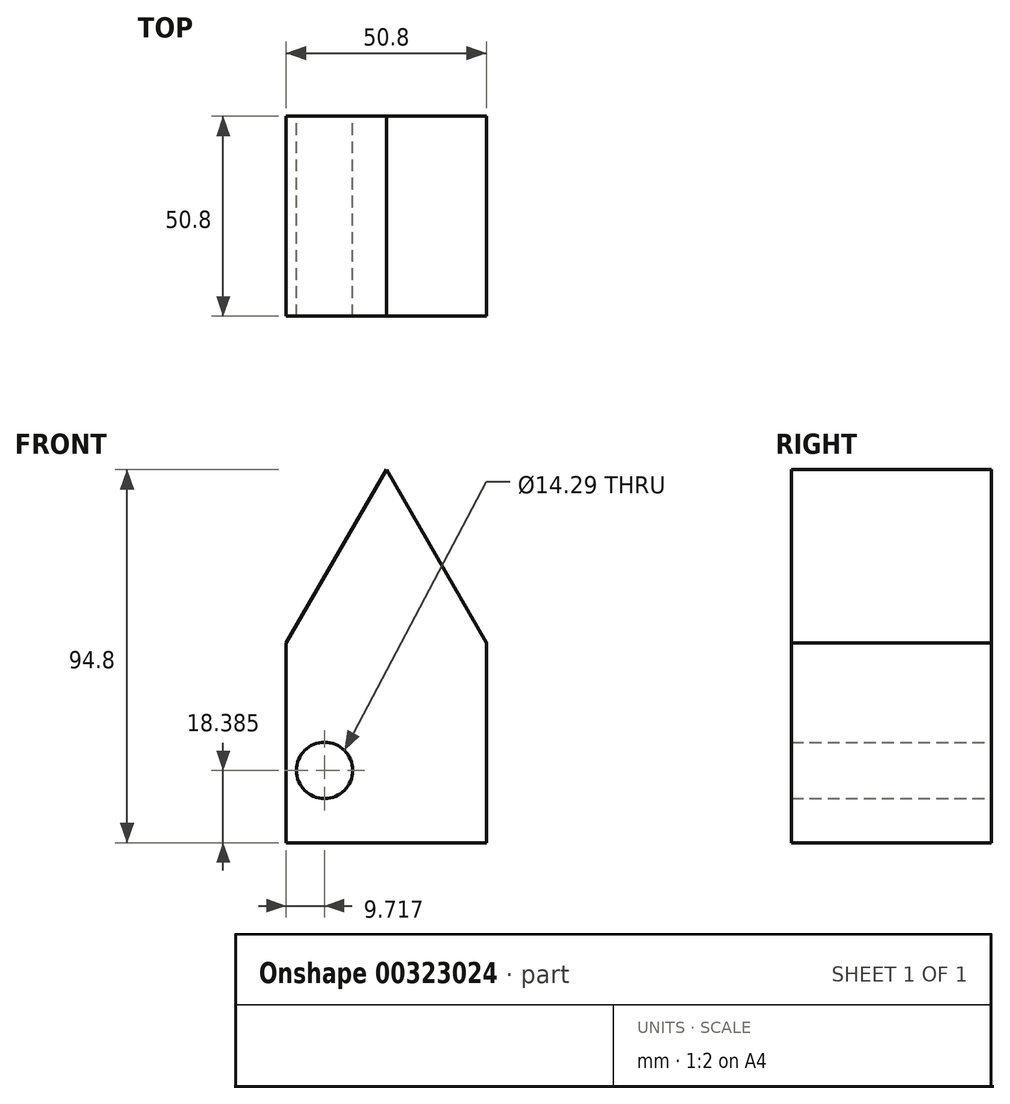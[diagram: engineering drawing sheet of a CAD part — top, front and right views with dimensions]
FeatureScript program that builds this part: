
annotation { "Feature Type Name" : "Feature", "Feature Type Description" : "" }
export const myFeature = defineFeature(function(context is Context, id is Id, definition is map)
    precondition{}
    {
        {
            var Q0;
            Q0=qCreatedBy(makeId("Front.planeOp"),FACE);
            var sketch = newSketch(context, id + "F0", { "sketchPlane" : qUnion([Q0])});
            skLineSegment(sketch, "E0.top", {"start": v(-25.4, -26.88) * mm, "end": v(25.4, -26.88) * mm});
            skLineSegment(sketch, "E0.left", {"start": v(-25.4, 23.92) * mm, "end": v(-25.4, -26.88) * mm});
            skLineSegment(sketch, "E0.right", {"start": v(25.4, 23.92) * mm, "end": v(25.4, -26.88) * mm});
            skLineSegment(sketch, "E1", {"start": v(-25.4, 23.92) * mm, "end": v(0, 67.92) * mm});
            skLineSegment(sketch, "E2", {"start": v(0, 67.92) * mm, "end": v(25.4, 23.92) * mm});
            skCircle(sketch, "E3", {"center": v(-15.68, -8.5) * mm, "radius": 7.14 * mm});
            skSolve(sketch);
        }
        {
            var Q0;
            Q0=makeQuery(id+"F0.imprint","IMPRINT",FACE,{"disambiguationData":[TD([[makeQuery(id+"F0.imprint","IMPRINT",EDGE,{"derivedFrom":sQuery(id+"F0.wireOp",EDGE,"E0.top")}),1.0]])]});
            extrude(context, id + "F1", {"entities" : qUnion([Q0]), "depth" : 50.8 * mm});
        }
    });
